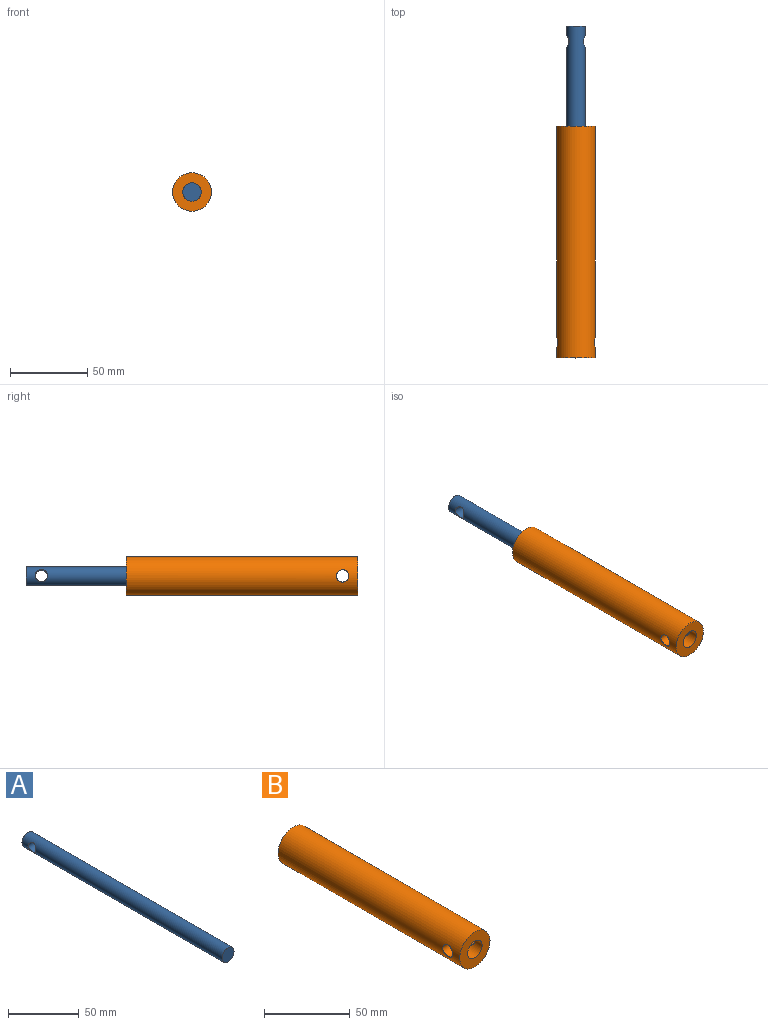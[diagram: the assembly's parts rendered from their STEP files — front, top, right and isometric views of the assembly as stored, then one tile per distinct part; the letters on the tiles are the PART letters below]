
ASSEMBLY  parts=2 mates=1
PART A: 4 faces, bbox 12x200x12 mm
  f0: cylinder r=6mm len=200mm, axis (0,1,0), area 7432.5mm2, adj f1,f2,f3
  f1: plane 12x12mm, normal (0,-1,0), area 113.1mm2, adj f0
  f2: plane 12x12mm, normal (0,1,0), area 113.1mm2, adj f0
  f3: cylinder r=4mm len=12mm, axis (1,0,0), area 264.6mm2, adj f0
PART B: 6 faces, bbox 25x150x25 mm
  f0: cylinder r=6mm len=150mm, axis (0,-1,0), area 5547.5mm2, adj f2,f3,f4,f5
  f1: cylinder r=12.5mm len=150mm, axis (0,-1,0), area 11679mm2, adj f2,f3,f4,f5
  f2: plane 25x25mm, normal (0,1,0), area 377.8mm2, adj f0,f1
  f3: plane 25x25mm, normal (0,-1,0), area 377.8mm2, adj f0,f1
  f4: cylinder r=4mm len=8.03mm, axis (1,0,0), area 173.7mm2, adj f0,f1
  f5: cylinder r=4mm len=8.03mm, axis (1,0,0), area 173.7mm2, adj f0,f1
PLACE A rot(axis=(0,-1,0),176.9deg) t=(113.43,284.53,-1.78)mm
PLACE B t=(113.43,89.53,-1.78)mm fixed
MATE cylindrical A.f0 <-> B.f1  axis (0,1,0) through (113.43,94.53,-1.78)mm
